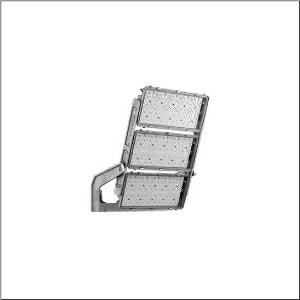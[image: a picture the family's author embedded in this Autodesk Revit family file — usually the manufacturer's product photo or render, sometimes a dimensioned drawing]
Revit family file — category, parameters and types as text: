
# Revit family: floodlight_fl_11_maxi_pro_remote___pl43_5xa779425a01aa_2185
name_source: partatom
category: Lighting Fixtures
units: mm (PartAtom-declared; Revit-internal decimal feet)

## family parameters
Cut with Voids When Loaded = No
Host = Face
Light Source = No
Part Type = Normal
Room Calculation Point = No
Round Connector Dimension = Use Diameter
Shared = No

## types (1)
- --- (1 x LED, 162210 lm, 1334.7 W, 3000K)
    Apparent Load = 1335 VA
    CIE Flux Codes = 25 74 99 100 100
    Color Rendering = 70
    Color Temperature = 3000K
    Default Elevation = 1800 mm
    Description = Floodlight FL 11  maxi  pro Remote floodlight; light control with lens of PMMA; cover panel of toughened safety glass, transparent; light distribution: PL43, asymmetric direct distribution, LEDcolour temperature: 3000K, rated luminous flux: 162.210lm, colour rendering: CRI > 70, light colour: 730; luminous efficacy: 122lm/W; brightness control: DALI 2 (1 DALI address); with terminal, 8-pole, max. 2.5mm², mains connection: 220..240V/380..400V AC, 50/60Hz, surge voltage resistance: line to ground: 10kV, ECG replaceable separately, LED unit replaceable without ESD environment, dustproof LED module, dimming range 10..100%, no afterglow with DALI off / DMX off command; 1335W floodlight with 2x LED unit of diecast aluminium, coated grey; length: 713mm / width: 651mm / height: 338mm; mounting bracket, of diecast aluminium, uncoated, natural, equipment: Power, protection rating (complete): IP66; insulation class (complete): insulation class I (protective earthing); certification: CE, ENEC, VDE; ball protection: ball impact resistance with accessories, impact resistance: IK07; rated ambient temperature 10°C, only for outdoor installations, permissible operating ambient temperature: -40..+30°C, permissible storage temperature: -40..+85°Cpackaging unit: 1 piece

Light Distribution: PL43
    Height = 320 mm
    Lamp = 1 x LED
    Lamp Light Flux = 162210 lm
    Lamp Power = 1334.7 W
    Lamp count = 1
    Length = 1002 mm
    Luminous efficacy = 122 lm/W
    Manufacturer = Siteco
    ModVariant = No
    Model = 5XA779425A01AA
    Mounting Place = Ceiling
    Mounting Type = Surface mounted
    Number of Poles = 1
    OnlyDefault = Yes
    Power Factor = 1
    Product Name = Floodlight FL 11 maxi pro Remote | PL43
    Product group = floodlight | ceiling mounted
    ProductGroupID = 301
    Protection Class = Protection class I
    Protection Degree = IP 66
    RLX_Detail_Level = 1
    RLX_Emergency_Light_Flux = 0 lm
    RLX_Emergency_Type = 0
    RLX_Emergency_Type_DB = No
    RlxData = <blob elided: 52313 chars, md5=0609a26f>
    Socket = socket
    Standby Power = 0 W
    System Light Flux = 162210 lm
    System Power = 1335 W
    Type Comments = factory setting: luminous flux: 100 % | dim-lin: 254 | 920 mA
    Type Image = l_1349141.jpg
    URL = http://relux.com
    VarID = @adj_096260
    Voltage = 0 V
    Weight = 0.00 kg
    Width = 655 mm

## geometry (parser evidence)
native form markers: Blend x4, Sweep x13
no freeform markers — native parametric forms only
